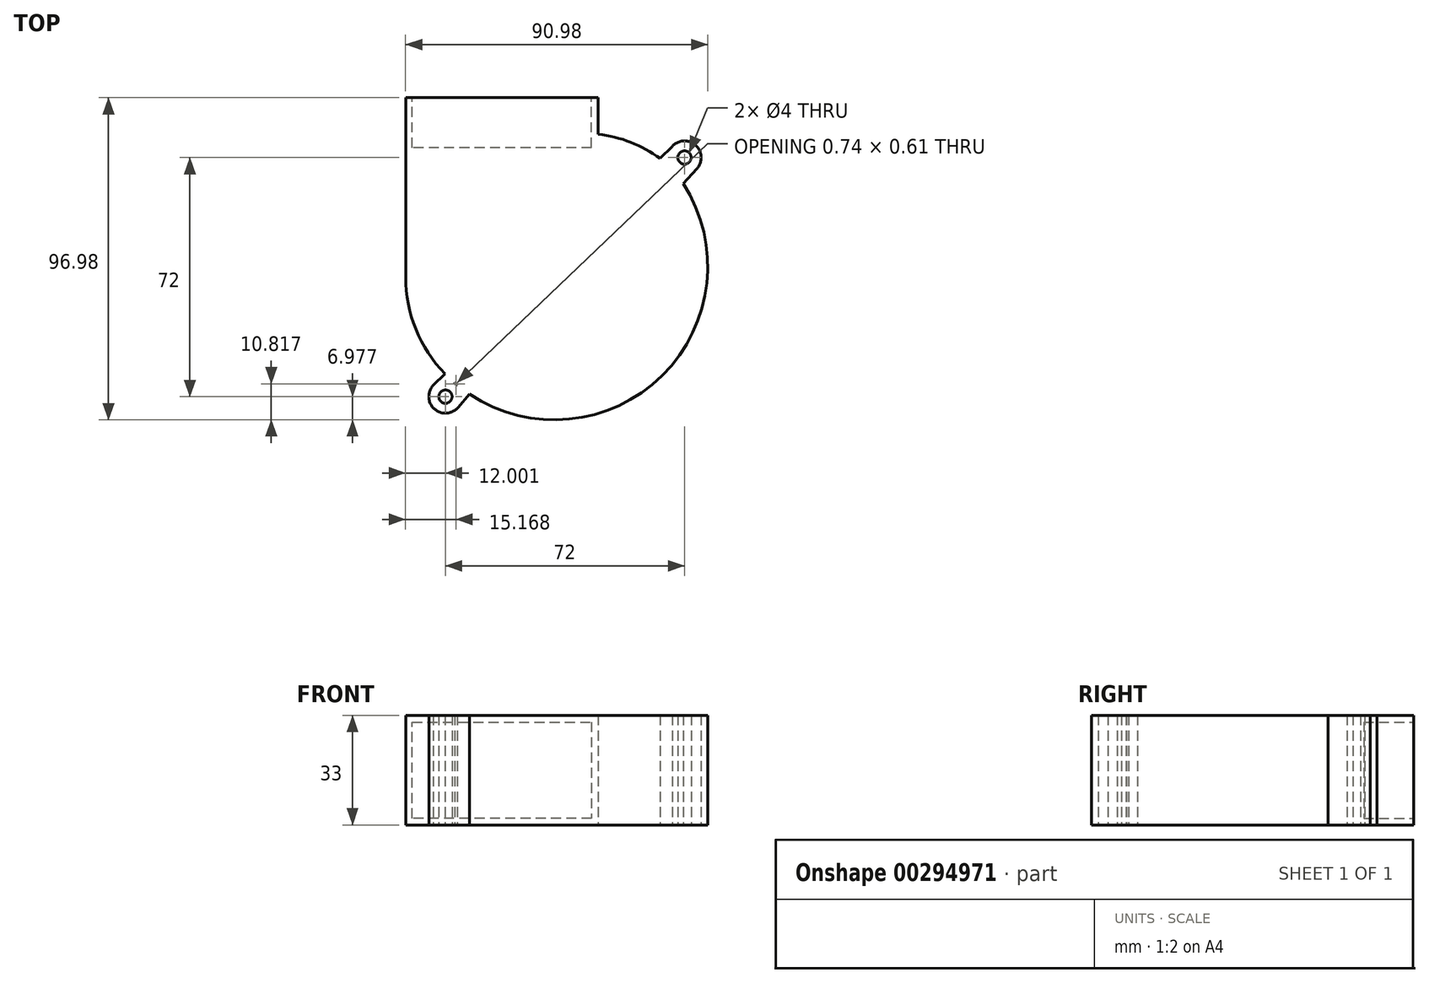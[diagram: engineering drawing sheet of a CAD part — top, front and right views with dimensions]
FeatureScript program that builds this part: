
annotation { "Feature Type Name" : "Feature", "Feature Type Description" : "" }
export const myFeature = defineFeature(function(context is Context, id is Id, definition is map)
    precondition{}
    {
        {
            var Q0;
            Q0=qCreatedBy(makeId("Top.planeOp"),FACE);
            var sketch = newSketch(context, id + "F0", { "sketchPlane" : qUnion([Q0])});
            skLineSegment(sketch, "E0", {"start": v(-19.89, 50.46) * mm, "end": v(38.11, 50.46) * mm});
            skLineSegment(sketch, "E1", {"start": v(38.11, 50.46) * mm, "end": v(38.11, 39.46) * mm});
            skLineSegment(sketch, "E2", {"start": v(-19.89, 50.46) * mm, "end": v(-19.89, -3.54) * mm});
            skPoint(sketch, "E3", {"position": v(-7.89, -39.54) * mm});
            skPoint(sketch, "E4", {"position": v(64.11, 32.46) * mm});
            skArc(sketch, "E5", {"start": v(67.78, 29.06) * mm, "mid": v(67.48, 36.16) * mm, "end": v(60.38, 35.79) * mm});
            skArc(sketch, "E6", {"start": v(-4.35, -36) * mm, "mid": v(-4.7, -35.69) * mm, "end": v(-5.1, -35.4) * mm});
            skPoint(sketch, "E7.third.point", {"position": v(67.3, 8.07) * mm});
            skArc(sketch, "E8", {"start": v(-19.89, -3.54) * mm, "mid": v(-16.82, -19.24) * mm, "end": v(-8.07, -32.63) * mm});
            skArc(sketch, "E9", {"start": v(-0.59, -38.8) * mm, "mid": v(57.37, -33.23) * mm, "end": v(63.7, 24.65) * mm});
            skArc(sketch, "E10", {"start": v(56.73, 32.17) * mm, "mid": v(47.9, 37.05) * mm, "end": v(38.11, 39.46) * mm});
            skLineSegment(sketch, "E11", {"start": v(63.7, 24.65) * mm, "end": v(67.78, 29.06) * mm});
            skLineSegment(sketch, "E12", {"start": v(60.38, 35.79) * mm, "end": v(56.73, 32.17) * mm});
            skLineSegment(sketch, "E13", {"start": v(-11.55, -36.14) * mm, "end": v(-8.07, -32.63) * mm});
            skLineSegment(sketch, "E14", {"start": v(-4.13, -42.84) * mm, "end": v(-0.59, -38.8) * mm});
            skArc(sketch, "E15.trimOffspring", {"start": v(-5.1, -35.4) * mm, "mid": v(-4.72, -35.7) * mm, "end": v(-4.35, -36) * mm});
            skArc(sketch, "E16.trimOffspring", {"start": v(-11.32, -35.9) * mm, "mid": v(-11.36, -43.14) * mm, "end": v(-4.13, -42.84) * mm});
            skCircle(sketch, "E17", {"center": v(64.11, 32.46) * mm, "radius": 2 * mm});
            skCircle(sketch, "E18", {"center": v(-7.89, -39.54) * mm, "radius": 2 * mm});
            skSolve(sketch);
        }
        {
            var Q0;
            Q0=makeQuery(id+"F0.imprint","IMPRINT",FACE,{"disambiguationData":[TD([[makeQuery(id+"F0.imprint","IMPRINT",EDGE,{"derivedFrom":sQuery(id+"F0.wireOp",EDGE,"E0")}),-1.0]])]});
            extrude(context, id + "F1", {"entities" : qUnion([Q0]), "depth" : 33 * mm});
        }
        {
            var Q0;
            Q0=makeQuery(id+"F1.opExtrude","SWEPT_FACE",FACE,{"disambiguationData":[OSD([sQuery(id+"F0.wireOp",EDGE,"E0")])]});
            var sketch = newSketch(context, id + "F2", { "sketchPlane" : qUnion([Q0])});
            skLineSegment(sketch, "E19.0", {"start": v(-36.11, 2) * mm, "end": v(17.89, 2) * mm});
            skLineSegment(sketch, "E19.1", {"start": v(-36.11, 31) * mm, "end": v(-36.11, 2) * mm});
            skLineSegment(sketch, "E19.2", {"start": v(17.89, 31) * mm, "end": v(-36.11, 31) * mm});
            skLineSegment(sketch, "E19.3", {"start": v(17.89, 2) * mm, "end": v(17.89, 31) * mm});
            skSolve(sketch);
        }
        {
            var Q0;
            Q0=makeQuery(id+"F2.imprint","IMPRINT",FACE,{"disambiguationData":[TD([[makeQuery(id+"F2.imprint","IMPRINT",EDGE,{"derivedFrom":sQuery(id+"F2.wireOp",EDGE,"E19.0")}),1.0]])]});
            extrude(context, id + "F3", {"entities" : qUnion([Q0]), "operationType" : NewBodyOperationType.REMOVE, "oppositeDirection" : true, "depth" : 15 * mm});
        }
    });
